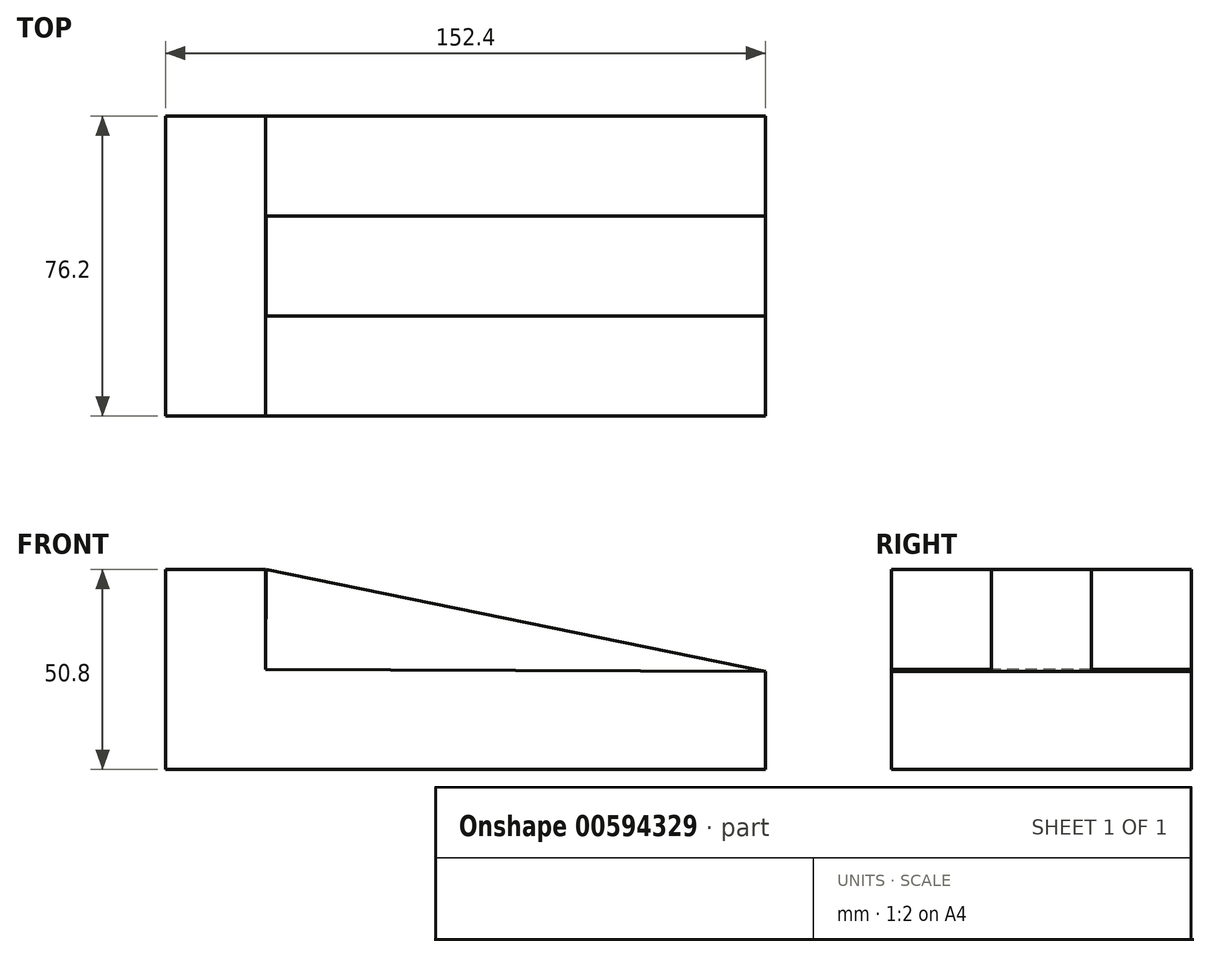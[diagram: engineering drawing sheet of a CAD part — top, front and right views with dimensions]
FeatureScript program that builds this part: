
annotation { "Feature Type Name" : "Feature", "Feature Type Description" : "" }
export const myFeature = defineFeature(function(context is Context, id is Id, definition is map)
    precondition{}
    {
        {
            var Q0;
            Q0=qCreatedBy(makeId("Front.planeOp"),FACE);
            var sketch = newSketch(context, id + "F0", { "sketchPlane" : qUnion([Q0])});
            skLineSegment(sketch, "E0", {"start": v(0, 0) * mm, "end": v(0, 50.8) * mm});
            skLineSegment(sketch, "E1", {"start": v(0, 50.8) * mm, "end": v(25.4, 50.8) * mm});
            skLineSegment(sketch, "E2", {"start": v(25.4, 50.8) * mm, "end": v(152.4, 24.88) * mm});
            skLineSegment(sketch, "E3", {"start": v(152.4, 24.88) * mm, "end": v(152.4, 0) * mm});
            skLineSegment(sketch, "E4", {"start": v(152.4, 0) * mm, "end": v(0, 0) * mm});
            skLineSegment(sketch, "E5", {"start": v(25.4, 50.8) * mm, "end": v(25.4, 25.4) * mm});
            skLineSegment(sketch, "E6", {"start": v(25.4, 25.4) * mm, "end": v(152.4, 24.88) * mm});
            skSolve(sketch);
        }
        {
            var Q0;
            Q0=makeQuery(id+"F0.imprint","IMPRINT",FACE,{"disambiguationData":[TD([[makeQuery(id+"F0.imprint","IMPRINT",EDGE,{"derivedFrom":sQuery(id+"F0.wireOp",EDGE,"E0")}),-1.0]])]});
            extrude(context, id + "F1", {"entities" : qUnion([Q0]), "oppositeDirection" : true, "depth" : 76.2 * mm, "offsetDistance" : 25.4 * mm});
        }
        {
            var Q0;
            Q0=makeQuery(id+"F1.opExtrude","SWEPT_FACE",FACE,{"disambiguationData":[OSD([sQuery(id+"F0.wireOp",EDGE,"E6")])]});
            var sketch = newSketch(context, id + "F2", { "sketchPlane" : qUnion([Q0])});
            skLineSegment(sketch, "E7", {"start": v(25.3, 50.8) * mm, "end": v(152.3, 50.8) * mm});
            skLineSegment(sketch, "E8", {"start": v(152.3, 50.8) * mm, "end": v(152.3, 25.4) * mm});
            skLineSegment(sketch, "E9", {"start": v(25.3, 25.4) * mm, "end": v(152.3, 25.4) * mm});
            skLineSegment(sketch, "E10", {"start": v(25.3, 25.4) * mm, "end": v(25.3, 50.8) * mm});
            skSolve(sketch);
        }
        {
            var Q0;
            Q0=makeQuery(id+"F2.imprint","IMPRINT",FACE,{"disambiguationData":[TD([[makeQuery(id+"F2.imprint","IMPRINT",EDGE,{"derivedFrom":sQuery(id+"F2.wireOp",EDGE,"E7")}),-1.0]])]});
            extrude(context, id + "F3", {"entities" : qUnion([Q0]), "operationType" : NewBodyOperationType.ADD, "depth" : 25.4 * mm, "offsetDistance" : 25.4 * mm});
        }
        {
            var Q0;
            Q0=makeQuery(id+"F3.opExtrude","SWEPT_FACE",FACE,{"disambiguationData":[OSD([sQuery(id+"F2.wireOp",EDGE,"E9")])]});
            var sketch = newSketch(context, id + "F4", { "sketchPlane" : qUnion([Q0])});
            skPoint(sketch, "E11", {"position": v(25.5, 50.8) * mm});
            skPoint(sketch, "E12", {"position": v(152.4, 24.88) * mm});
            skLineSegment(sketch, "E13", {"start": v(25.5, 50.8) * mm, "end": v(152.4, 24.88) * mm});
            skPoint(sketch, "E14", {"position": v(152.5, 50.28) * mm});
            skLineSegment(sketch, "E15", {"start": v(152.5, 50.28) * mm, "end": v(152.4, 24.88) * mm});
            skLineSegment(sketch, "E16", {"start": v(152.5, 50.28) * mm, "end": v(25.5, 50.8) * mm});
            skSolve(sketch);
        }
        {
            var Q0;
            Q0=makeQuery(id+"F4.imprint","IMPRINT",FACE,{"disambiguationData":[TD([[makeQuery(id+"F4.imprint","IMPRINT",EDGE,{"derivedFrom":sQuery(id+"F4.wireOp",EDGE,"E13")}),1.0]])]});
            extrude(context, id + "F5", {"entities" : qUnion([Q0]), "operationType" : NewBodyOperationType.REMOVE, "oppositeDirection" : true, "depth" : 25.4 * mm, "offsetDistance" : 25.4 * mm});
        }
    });
